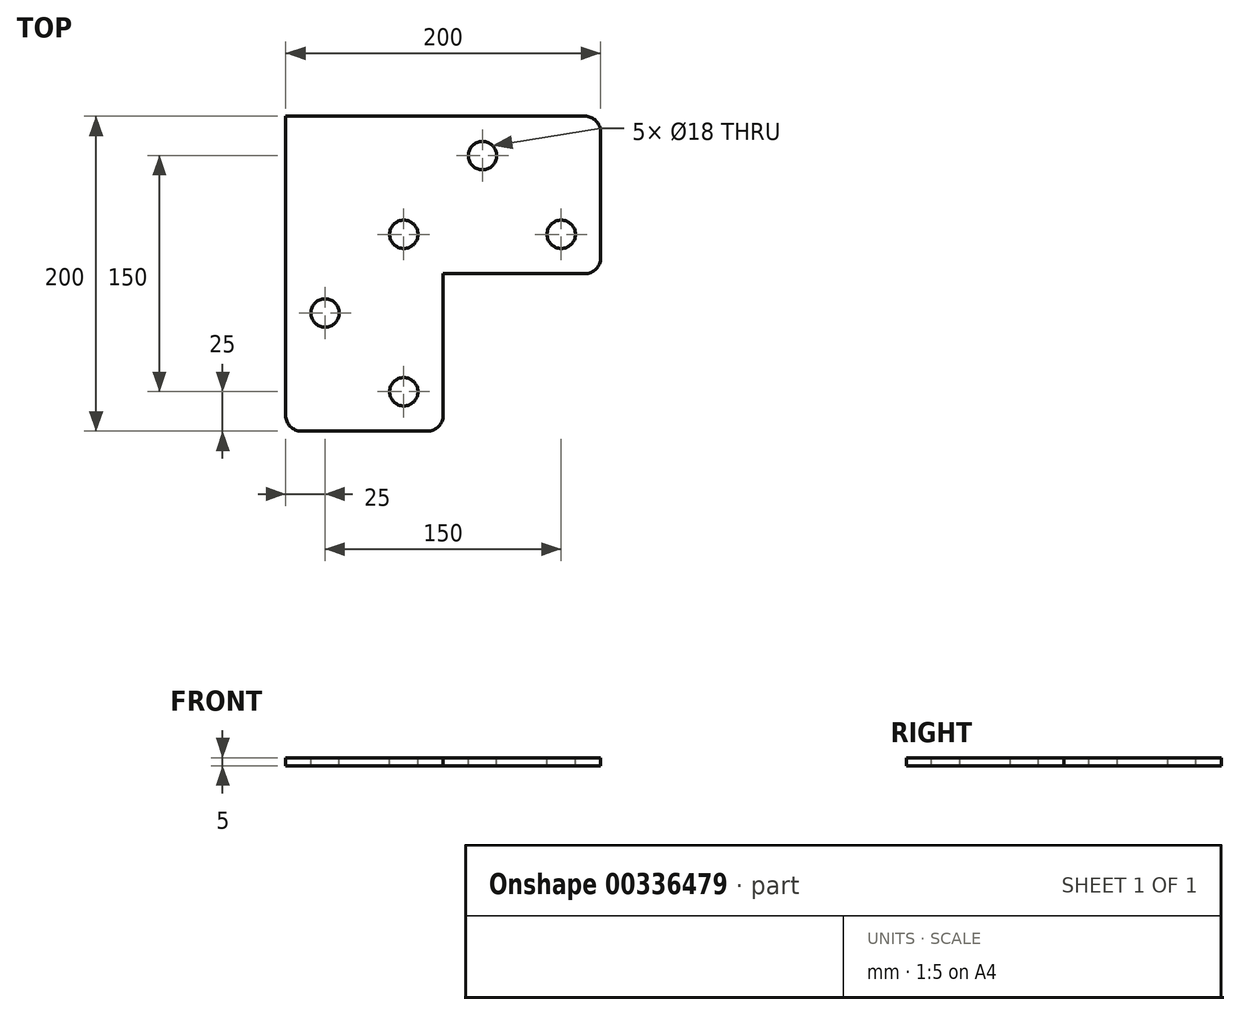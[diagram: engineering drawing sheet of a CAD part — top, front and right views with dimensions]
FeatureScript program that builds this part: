
annotation { "Feature Type Name" : "Feature", "Feature Type Description" : "" }
export const myFeature = defineFeature(function(context is Context, id is Id, definition is map)
    precondition{}
    {
        {
            var Q0;
            Q0=qCreatedBy(makeId("Top.planeOp"),FACE);
            var sketch = newSketch(context, id + "F0", { "sketchPlane" : qUnion([Q0])});
            skLineSegment(sketch, "E0", {"start": v(0, 0) * mm, "end": v(200, 0) * mm});
            skLineSegment(sketch, "E1", {"start": v(200, 0) * mm, "end": v(200, -100) * mm});
            skLineSegment(sketch, "E2", {"start": v(200, -100) * mm, "end": v(100, -100) * mm});
            skLineSegment(sketch, "E3", {"start": v(100, -100) * mm, "end": v(100, -200) * mm});
            skLineSegment(sketch, "E4", {"start": v(100, -200) * mm, "end": v(0, -200) * mm});
            skLineSegment(sketch, "E5", {"start": v(0, -200) * mm, "end": v(0, 0) * mm});
            skSolve(sketch);
        }
        {
            var Q0;
            Q0=makeQuery(id+"F0.imprint","IMPRINT",FACE,{"disambiguationData":[TD([[makeQuery(id+"F0.imprint","IMPRINT",EDGE,{"derivedFrom":sQuery(id+"F0.wireOp",EDGE,"E0")}),-1.0]])]});
            extrude(context, id + "F1", {"entities" : qUnion([Q0]), "depth" : 5 * mm});
        }
        {
            var Q0;
            Q0=makeQuery(id+"F1.opExtrude","CAP_FACE",FACE,{"disambiguationData":[OSD([sQuery(id+"F0.wireOp",EDGE,"E0"),sQuery(id+"F0.wireOp",EDGE,"E1"),sQuery(id+"F0.wireOp",EDGE,"E2"),sQuery(id+"F0.wireOp",EDGE,"E3"),sQuery(id+"F0.wireOp",EDGE,"E4"),sQuery(id+"F0.wireOp",EDGE,"E5")])],"isStart":false});
            var sketch = newSketch(context, id + "F2", { "sketchPlane" : qUnion([Q0])});
            skLineSegment(sketch, "E6.direction2", {"start": v(175, -25) * mm, "end": v(175, -75) * mm, "construction": true});
            skPoint(sketch, "E7.startSnap0", {"position": v(175, -50) * mm});
            skCircle(sketch, "E8.MirrorC", {"center": v(175, -75) * mm, "radius": 9 * mm});
            skCircle(sketch, "E9.MirrorC", {"center": v(125, -25) * mm, "radius": 9 * mm});
            skCircle(sketch, "E10.MirrorC", {"center": v(75, -75) * mm, "radius": 9 * mm});
            skCircle(sketch, "E11.MirrorC", {"center": v(75, -175) * mm, "radius": 9 * mm});
            skCircle(sketch, "E12.MirrorC", {"center": v(25, -125) * mm, "radius": 9 * mm});
            skLineSegment(sketch, "E13", {"start": v(-0.08, 0) * mm, "end": v(-51.97, 0) * mm});
            skLineSegment(sketch, "E14", {"start": v(-0.08, 0) * mm, "end": v(-0.08, 38.5) * mm});
            skSolve(sketch);
        }
        {
            var Q0;
            Q0 = qSketchRegion(id + "F2", true);
            extrude(context, id + "F3", {"entities" : qUnion([Q0]), "operationType" : NewBodyOperationType.REMOVE, "oppositeDirection" : true, "depth" : 25 * mm});
        }
        {
            var Q0;
            Q0=makeQuery(id+"F1.opExtrude","SWEPT_EDGE",EDGE,{"disambiguationData":[OSD([sQuery(id+"F0.wireOp",EDGE,"E4"),sQuery(id+"F0.wireOp",EDGE,"E5")])]});
            var Q1;
            Q1=makeQuery(id+"F1.opExtrude","SWEPT_EDGE",EDGE,{"disambiguationData":[OSD([sQuery(id+"F0.wireOp",EDGE,"E3"),sQuery(id+"F0.wireOp",EDGE,"E4")])]});
            var Q2;
            Q2=makeQuery(id+"F1.opExtrude","SWEPT_EDGE",EDGE,{"disambiguationData":[OSD([sQuery(id+"F0.wireOp",EDGE,"E1"),sQuery(id+"F0.wireOp",EDGE,"E2")])]});
            var Q3;
            Q3=makeQuery(id+"F1.opExtrude","SWEPT_EDGE",EDGE,{"disambiguationData":[OSD([sQuery(id+"F0.wireOp",EDGE,"E0"),sQuery(id+"F0.wireOp",EDGE,"E1")])]});
            fillet(context, id + "F4", {"entities" : qUnion([Q0, Q1, Q2, Q3]), "radius" : 10 * mm, "tangentPropagation" : true, "allowEdgeOverflow" : false});
        }
    });
